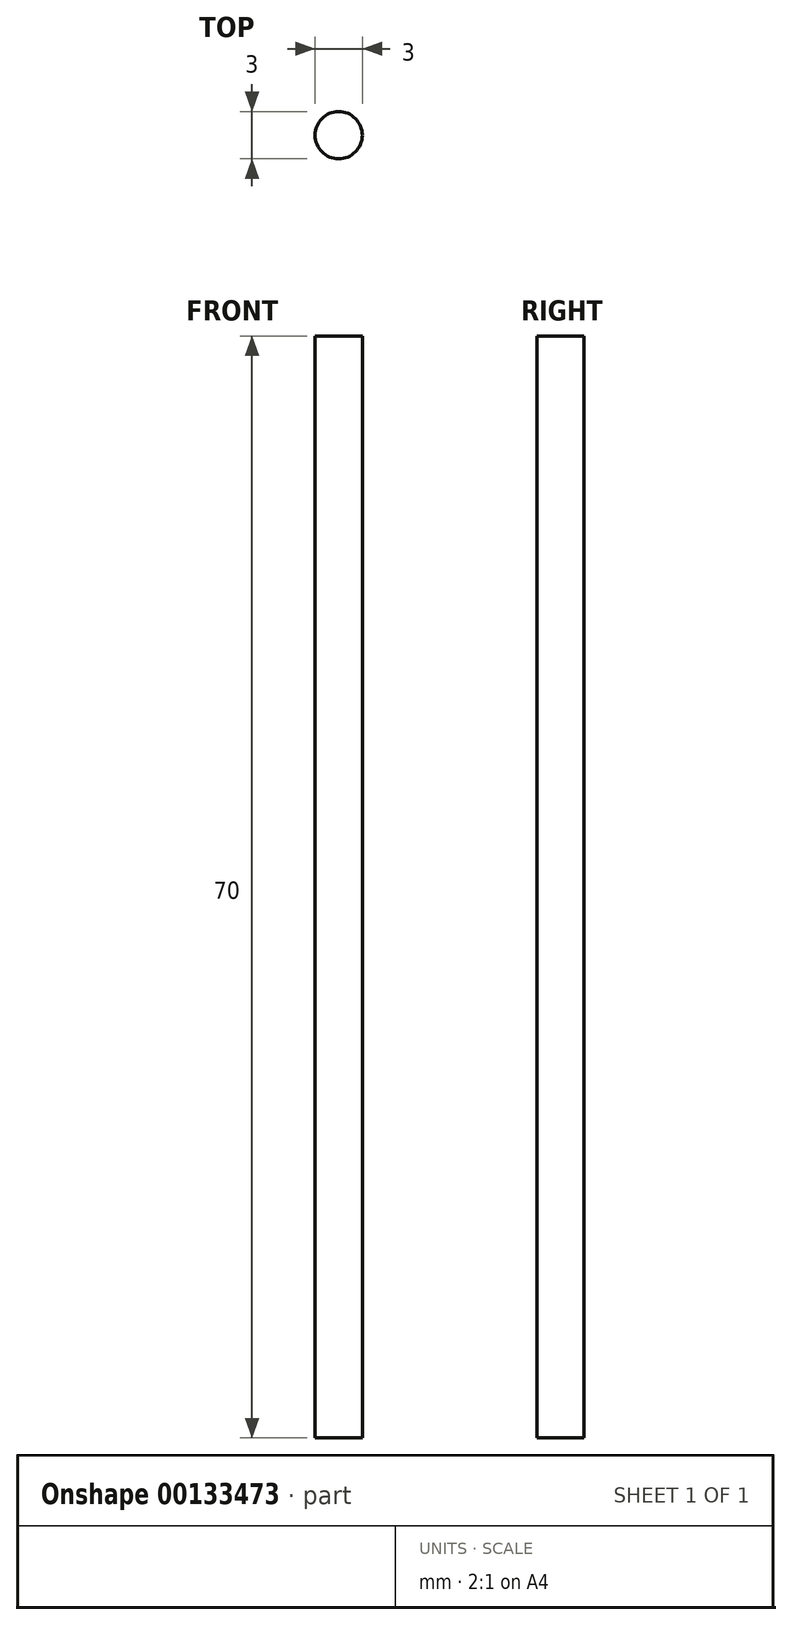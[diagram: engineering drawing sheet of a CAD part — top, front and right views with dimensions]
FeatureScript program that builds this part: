
annotation { "Feature Type Name" : "Feature", "Feature Type Description" : "" }
export const myFeature = defineFeature(function(context is Context, id is Id, definition is map)
    precondition{}
    {
        {
            var Q0;
            Q0=qCreatedBy(makeId("Top.planeOp"),FACE);
            var sketch = newSketch(context, id + "F0", { "sketchPlane" : qUnion([Q0])});
            skCircle(sketch, "E0", {"center": v(0, 0) * mm, "radius": 1.5 * mm});
            skSolve(sketch);
        }
        {
            var Q0;
            Q0=makeQuery(id+"F0.imprint","IMPRINT",FACE,{"disambiguationData":[TD([[makeQuery(id+"F0.imprint","IMPRINT",EDGE,{"derivedFrom":sQuery(id+"F0.wireOp",EDGE,"E0")}),1.0]])]});
            extrude(context, id + "F1", {"entities" : qUnion([Q0]), "depth" : 70 * mm});
        }
    });
